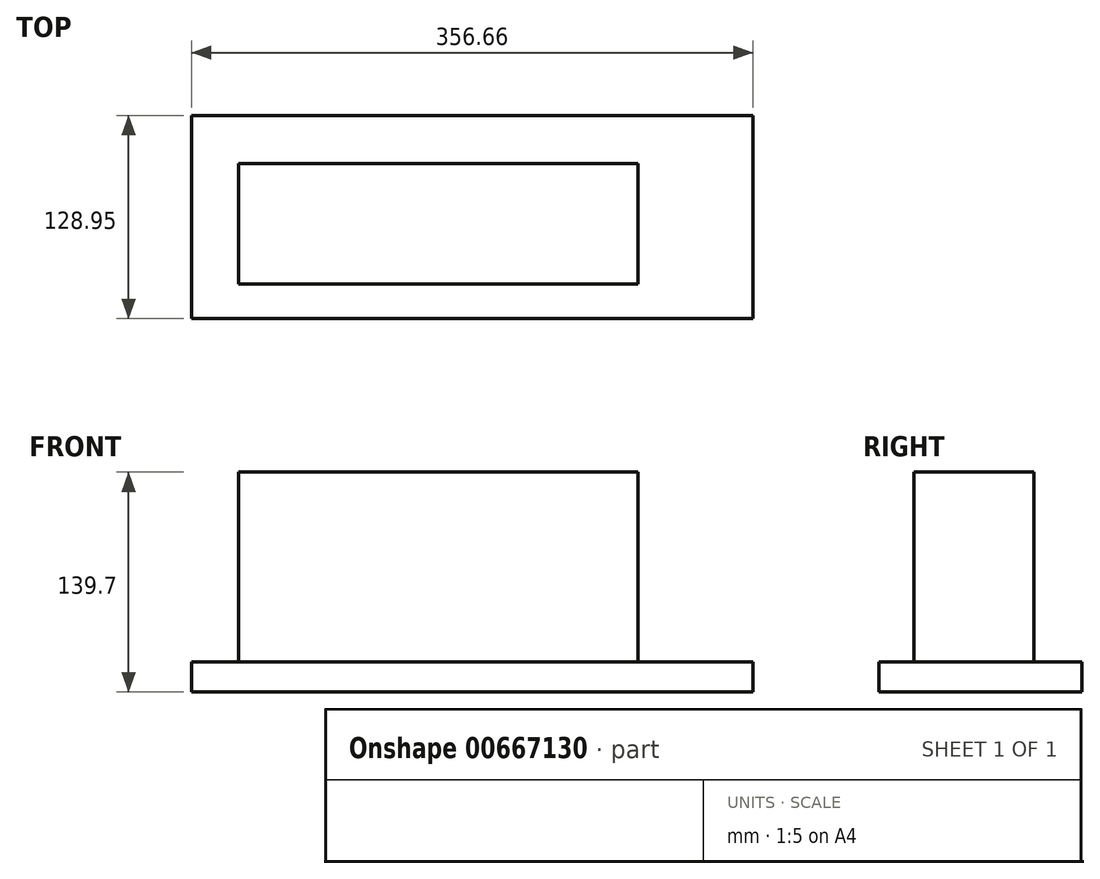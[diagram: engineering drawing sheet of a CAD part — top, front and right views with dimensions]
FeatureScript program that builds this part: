
annotation { "Feature Type Name" : "Feature", "Feature Type Description" : "" }
export const myFeature = defineFeature(function(context is Context, id is Id, definition is map)
    precondition{}
    {
        {
            var Q0;
            Q0=qCreatedBy(makeId("Top.planeOp"),FACE);
            var sketch = newSketch(context, id + "F0", { "sketchPlane" : qUnion([Q0])});
            skLineSegment(sketch, "E0.bottom", {"start": v(0, 0) * mm, "end": v(356.66, 0) * mm});
            skLineSegment(sketch, "E0.top", {"start": v(0, -128.95) * mm, "end": v(356.66, -128.95) * mm});
            skLineSegment(sketch, "E0.left", {"start": v(0, 0) * mm, "end": v(0, -128.95) * mm});
            skLineSegment(sketch, "E0.right", {"start": v(356.66, 0) * mm, "end": v(356.66, -128.95) * mm});
            skLineSegment(sketch, "E1.bottom", {"start": v(30.07, -30.6) * mm, "end": v(283.53, -30.6) * mm});
            skLineSegment(sketch, "E1.top", {"start": v(30.07, -106.88) * mm, "end": v(283.53, -106.88) * mm});
            skLineSegment(sketch, "E1.left", {"start": v(30.07, -30.6) * mm, "end": v(30.07, -106.88) * mm});
            skLineSegment(sketch, "E1.right", {"start": v(283.53, -30.6) * mm, "end": v(283.53, -106.88) * mm});
            skSolve(sketch);
        }
        {
            var Q0;
            Q0=makeQuery(id+"F0.imprint","IMPRINT",FACE,{"disambiguationData":[TD([[makeQuery(id+"F0.imprint","IMPRINT",EDGE,{"derivedFrom":sQuery(id+"F0.wireOp",EDGE,"E1.bottom")}),-1.0]])]});
            extrude(context, id + "F1", {"entities" : qUnion([Q0]), "depth" : 139.7 * mm, "offsetDistance" : 25.4 * mm});
        }
        {
            var Q0;
            Q0 = qSketchRegion(id + "F0", true);
            extrude(context, id + "F2", {"entities" : qUnion([Q0]), "operationType" : NewBodyOperationType.ADD, "depth" : 19.05 * mm, "offsetDistance" : 25.4 * mm});
        }
    });
